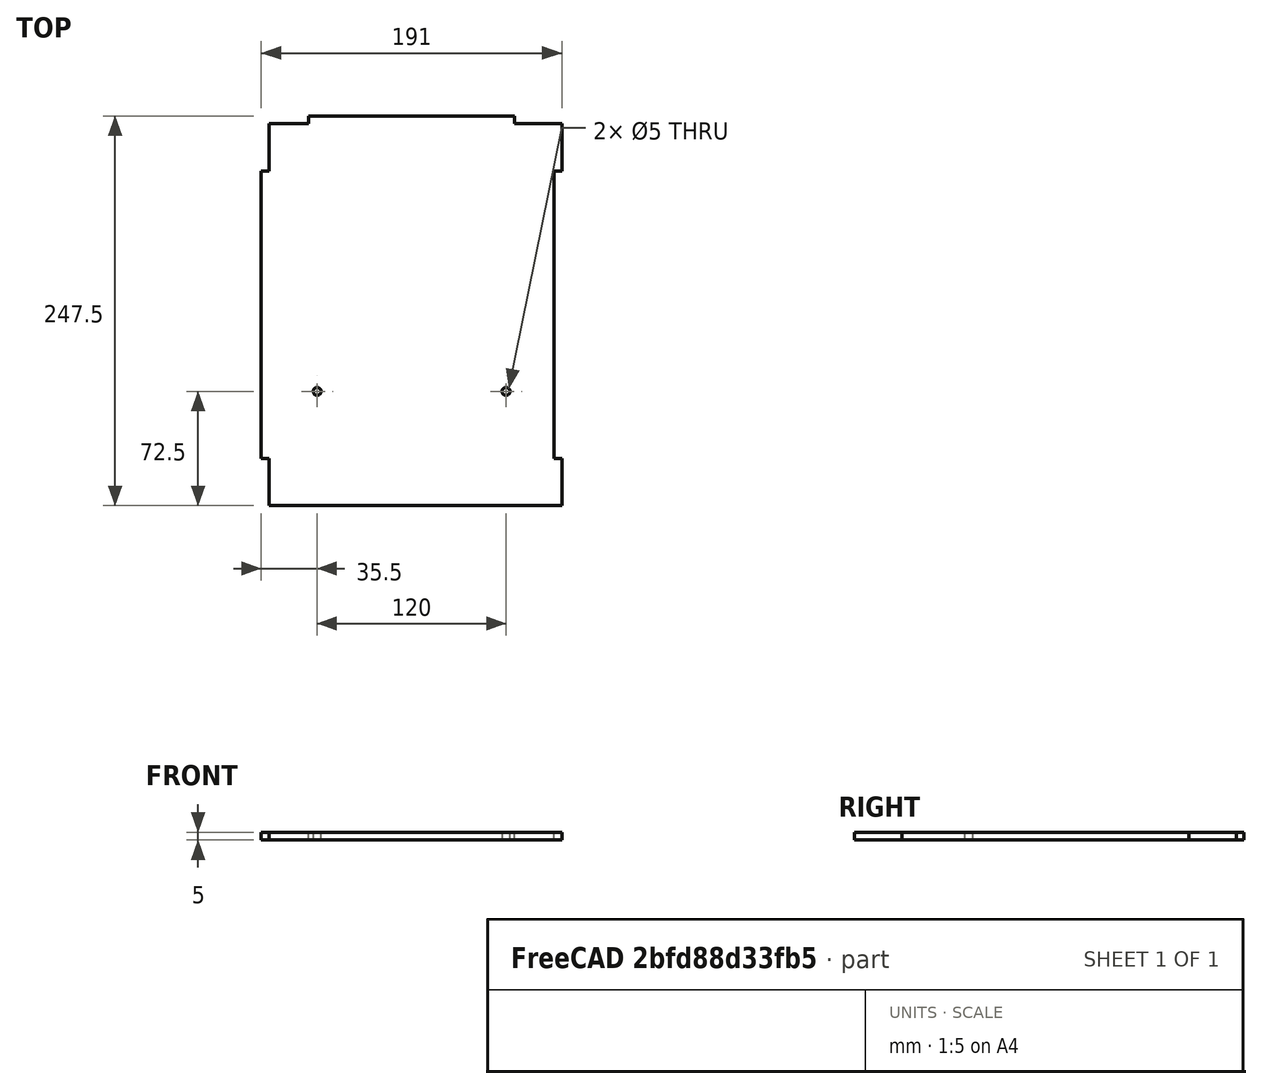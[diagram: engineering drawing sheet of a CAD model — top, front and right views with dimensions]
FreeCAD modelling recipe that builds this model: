
FCSTD DOCUMENT  (FreeCAD 0.15R4671 (Git))
Label: lower_side_axis_x2
License: All rights reserved
LicenseURL: http://en.wikipedia.org/wiki/All_rights_reserved
objects: Sketcher::SketchObject×1, PartDesign::Pad×1
note: 3 computed .brp shape members not serialized (recipe doc carries the construction recipe); baked Part::Feature solids carry a one-line shape summary decoded from their .brp

FEATURE [Sketcher::SketchObject] Sketch
  sketch-geometry (19):
    g0: LineSegment StartX=63 StartY=121.25 StartZ=0 EndX=93 EndY=121.25 EndZ=0
    g1: LineSegment StartX=93 StartY=121.25 StartZ=0 EndX=93 EndY=91.25 EndZ=0
    g2: LineSegment StartX=93 StartY=91.25 StartZ=0 EndX=88 EndY=91.25 EndZ=0
    g3: LineSegment StartX=88 StartY=91.25 StartZ=0 EndX=88 EndY=-91.25 EndZ=0
    g4: LineSegment StartX=88 StartY=-91.25 StartZ=0 EndX=93 EndY=-91.25 EndZ=0
    g5: LineSegment StartX=93 StartY=-91.25 StartZ=0 EndX=93 EndY=-121.25 EndZ=0
    g6: LineSegment StartX=93 StartY=-121.25 StartZ=0 EndX=-93 EndY=-121.25 EndZ=0
    g7: LineSegment StartX=-93 StartY=-121.25 StartZ=0 EndX=-93 EndY=-91.25 EndZ=0
    g8: LineSegment StartX=-93 StartY=-91.25 StartZ=0 EndX=-98 EndY=-91.25 EndZ=0
    g9: LineSegment StartX=-98 StartY=-91.25 StartZ=0 EndX=-98 EndY=91.25 EndZ=0
    g10: LineSegment StartX=-98 StartY=91.25 StartZ=0 EndX=-93 EndY=91.25 EndZ=0
    g11: LineSegment StartX=-93 StartY=91.25 StartZ=0 EndX=-93 EndY=121.25 EndZ=0
    g12: LineSegment StartX=-93 StartY=121.25 StartZ=0 EndX=-68 EndY=121.25 EndZ=0
    g13: LineSegment StartX=-68 StartY=121.25 StartZ=0 EndX=-68 EndY=126.25 EndZ=0
    g14: LineSegment StartX=-68 StartY=126.25 StartZ=0 EndX=63 EndY=126.25 EndZ=0
    g15: LineSegment StartX=63 StartY=126.25 StartZ=0 EndX=63 EndY=121.25 EndZ=0
    g16: Circle CenterX=57.5 CenterY=-48.75 CenterZ=0 NormalX=0 NormalY=0 NormalZ=1 Radius=2.5
    g17: Circle CenterX=-62.5 CenterY=-48.75 CenterZ=0 NormalX=0 NormalY=0 NormalZ=1 Radius=2.5
    g18: LineSegment [constr] StartX=-62.5 StartY=-48.75 StartZ=0 EndX=57.5 EndY=-48.75 EndZ=0
  constraints (56):
    c: Coincident(g13,g14)
    c: Coincident(g12,g13)
    c: Coincident(g11,g12)
    c: Coincident(g14,g15)
    c: Coincident(g0,g15)
    c: Coincident(g0,g1)
    c: Coincident(g1,g2)
    c: Coincident(g2,g3)
    c: Coincident(g4,g5)
    c: Coincident(g3,g4)
    c: Coincident(g5,g6)
    c: Coincident(g6,g7)
    c: Coincident(g7,g8)
    c: Coincident(g8,g9)
    c: Coincident(g9,g10)
    c: Coincident(g10,g11)
    c: Horizontal(g6)
    c: Horizontal(g8)
    c: Horizontal(g10)
    c: Horizontal(g12)
    c: Horizontal(g14)
    c: Horizontal(g0)
    c: Horizontal(g2)
    c: Horizontal(g4)
    c: Vertical(g5)
    c: Vertical(g3)
    c: Vertical(g7)
    c: Vertical(g9)
    c: Vertical(g11)
    c: Vertical(g13)
    c: Vertical(g15)
    c: Vertical(g1)
    c: Equal(g2,g4)
    c: Equal(g4,g8)
    c: Equal(g8,g10)
    c: DistanceX(g10) = 5
    c: DistanceX(g10,g2) = 181
    c: Equal(g0,g1)
    c: Equal(g1,g5)
    c: Equal(g5,g7)
    c: Equal(g7,g11)
    c: DistanceY(g1) = -30
    c: DistanceX(g12) = 25
    c: Equal(g17,g16)
    c: Radius(g16) = 2.5
    c: Coincident(g18,g17)
    c: Coincident(g18,g16)
    c: Horizontal(g18)
    c: DistanceX(g18) = 120
    c: DistanceX(g17,g7) = -30.5
    c: DistanceY(g17,g7) = -42.5
    c: Symmetric(g2,g3,g-1)
    c: Symmetric(g6,g5,g-2)
    c: Equal(g15,g2)
    c: Equal(g2,g13)
    c: DistanceY(g6,g12) = 242.5
FEATURE [PartDesign::Pad] Pad
  Length = 5
  Length2 = 100
  Midplane = true
  Sketch = -> Sketch
  Type = 0
